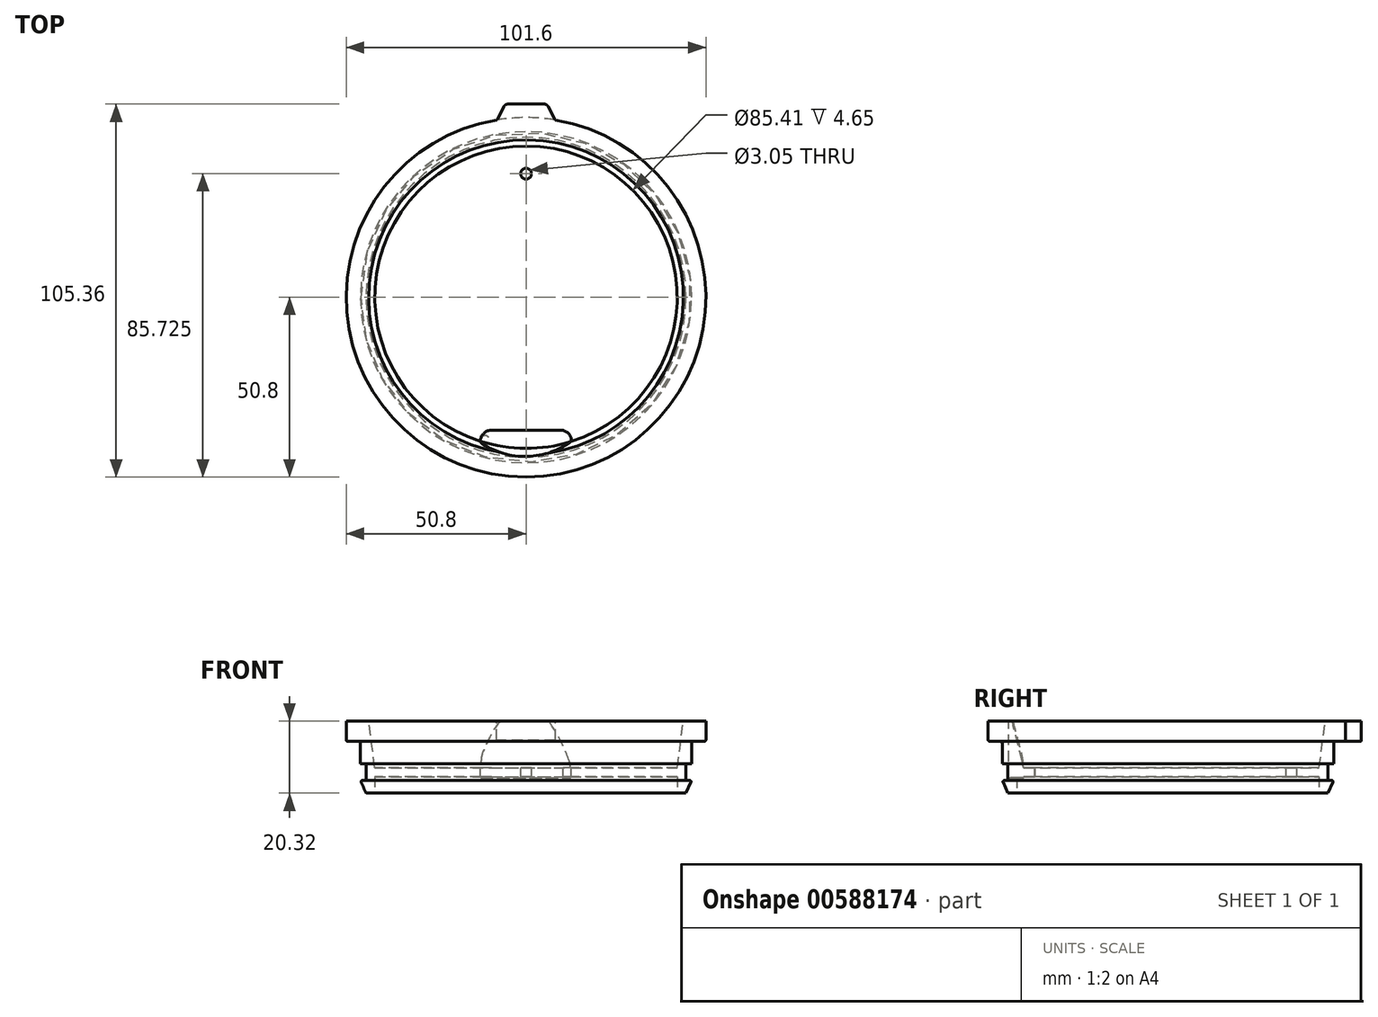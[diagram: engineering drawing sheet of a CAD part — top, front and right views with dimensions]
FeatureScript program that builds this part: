
annotation { "Feature Type Name" : "Feature", "Feature Type Description" : "" }
export const myFeature = defineFeature(function(context is Context, id is Id, definition is map)
    precondition{}
    {
        {
            var Q0;
            Q0=qCreatedBy(makeId("Front.planeOp"),FACE);
            var sketch = newSketch(context, id + "F0", { "sketchPlane" : qUnion([Q0])});
            skLineSegment(sketch, "E0", {"start": v(-44.45, 0) * mm, "end": v(-50.4, 0) * mm});
            skLineSegment(sketch, "E1", {"start": v(-50.8, -0.4) * mm, "end": v(-50.8, -5.24) * mm});
            skLineSegment(sketch, "E2", {"start": v(-50.4, -5.64) * mm, "end": v(-47.56, -5.64) * mm});
            skLineSegment(sketch, "E3", {"start": v(-46.78, -6.43) * mm, "end": v(-46.78, -12) * mm});
            skLineSegment(sketch, "E4", {"start": v(-46.78, -12) * mm, "end": v(-45.19, -12) * mm});
            skLineSegment(sketch, "E5", {"start": v(-45.19, -12) * mm, "end": v(-45.19, -16.76) * mm});
            skLineSegment(sketch, "E6", {"start": v(-45.19, -16.76) * mm, "end": v(-46.3, -16.76) * mm});
            skLineSegment(sketch, "E7", {"start": v(-45.19, -20.32) * mm, "end": v(-42.7, -20.32) * mm});
            skLineSegment(sketch, "E8", {"start": v(0, -20.32) * mm, "end": v(0, 0) * mm});
            skLineSegment(sketch, "E9", {"start": v(-46.58, -17.2) * mm, "end": v(-45.19, -20.32) * mm});
            skPoint(sketch, "E10.visualSharp", {"position": v(-46.78, -16.76) * mm});
            skArc(sketch, "E10.filletArc", {"start": v(-46.3, -16.76) * mm, "mid": v(-46.56, -16.9) * mm, "end": v(-46.58, -17.2) * mm});
            skPoint(sketch, "E11.visualSharp", {"position": v(-46.78, -5.64) * mm});
            skArc(sketch, "E11.filletArc", {"start": v(-46.78, -6.43) * mm, "mid": v(-47, -5.88) * mm, "end": v(-47.56, -5.64) * mm});
            skPoint(sketch, "E12.visualSharp", {"position": v(-50.8, -5.64) * mm});
            skArc(sketch, "E12.filletArc", {"start": v(-50.8, -5.24) * mm, "mid": v(-50.68, -5.53) * mm, "end": v(-50.4, -5.64) * mm});
            skPoint(sketch, "E13.visualSharp", {"position": v(-50.8, 0) * mm});
            skLineSegment(sketch, "E14", {"start": v(-44.45, 0) * mm, "end": v(-42.7, -13.13) * mm});
            skLineSegment(sketch, "E15", {"start": v(-42.7, -13.13) * mm, "end": v(0, -13.13) * mm});
            skLineSegment(sketch, "E16.0", {"start": v(-42.7, -15.67) * mm, "end": v(0, -15.67) * mm});
            skLineSegment(sketch, "E17", {"start": v(-42.7, -15.67) * mm, "end": v(-42.7, -20.32) * mm});
            skLineSegment(sketch, "E18", {"start": v(-50.8, -0.4) * mm, "end": v(-50.8, 0) * mm});
            skLineSegment(sketch, "E19", {"start": v(-50.4, 0) * mm, "end": v(-50.8, 0) * mm});
            skSolve(sketch);
        }
        {
            var Q0;
            Q0 = qSketchRegion(id + "F0", true);
            var Q1;
            Q1=sQuery(id+"F0.wireOp",EDGE,"E8");
            revolve(context, id + "F1", {"entities" : qUnion([Q0]), "axis" : qUnion([Q1]), "revolveType" : RevolveType.FULL});
        }
        {
            var Q0;
            Q0=makeQuery(id+"F1.opRevolve","SWEPT_FACE",FACE,{"disambiguationData":[OSD([sQuery(id+"F0.wireOp",EDGE,"E15")])]});
            cPlane(context, id + "F2", {"entities" : qUnion([Q0]), "cplaneType" : CPlaneType.OFFSET, "offset" : 0 * mm, "oppositeDirection" : true, "width" : 152.4 * mm, "height" : 152.4 * mm});
        }
        {
            var Q0;
            Q0=qCreatedBy(id+"F2.planeOp",FACE);
            var sketch = newSketch(context, id + "F3", { "sketchPlane" : qUnion([Q0])});
            skLineSegment(sketch, "E20", {"start": v(0, 0) * mm, "end": v(0, 34.93) * mm});
            skCircle(sketch, "E21", {"center": v(0, 34.93) * mm, "radius": 1.52 * mm});
            skLineSegment(sketch, "E22", {"start": v(0, 0) * mm, "end": v(0, -42.7) * mm});
            skLineSegment(sketch, "E23.0", {"start": v(-11.11, -37.55) * mm, "end": v(11.11, -37.64) * mm});
            skLineSegment(sketch, "E24", {"start": v(-11.11, -37.55) * mm, "end": v(-11.11, -40.72) * mm, "construction": true});
            skArc(sketch, "E25", {"start": v(-9.72, -37.55) * mm, "mid": v(-11.76, -38.29) * mm, "end": v(-12.86, -40.17) * mm});
            skArc(sketch, "E26.MirrorC", {"start": v(9.02, -37.64) * mm, "mid": v(11.25, -37.94) * mm, "end": v(12.72, -39.66) * mm});
            skPoint(sketch, "E27", {"position": v(-9.73, -43.9) * mm});
            skPoint(sketch, "E28", {"position": v(9.73, -43.9) * mm});
            skPoint(sketch, "E29.start.orphan", {"position": v(9.73, -45.46) * mm});
            skPoint(sketch, "E30.end.orphan", {"position": v(-9.73, -45.46) * mm});
            skArc(sketch, "E31", {"start": v(-12.28, -41.49) * mm, "mid": v(0.02, -44.99) * mm, "end": v(12.22, -41.17) * mm});
            skArc(sketch, "E32.filletArc", {"start": v(-12.86, -40.17) * mm, "mid": v(-12.77, -40.92) * mm, "end": v(-12.28, -41.49) * mm});
            skArc(sketch, "E33.filletArc", {"start": v(12.22, -41.17) * mm, "mid": v(12.73, -40.5) * mm, "end": v(12.72, -39.66) * mm});
            skSolve(sketch);
        }
        {
            var Q0;
            {var subQ0=sQuery(id+"F3.wireOp",EDGE,"E25");Q0=makeQuery(id+"F3.imprint","IMPRINT",FACE,{"disambiguationData":[TD([[makeQuery(id+"F3.imprint","IMPRINT",EDGE,{"derivedFrom":subQ0}),1.0]])]});}
            extrude(context, id + "F4", {"entities" : qUnion([Q0]), "operationType" : NewBodyOperationType.REMOVE, "oppositeDirection" : true, "depth" : 2.8 * mm, "offsetDistance" : 25.4 * mm});
        }
        {
            var Q0;
            Q0 = qSketchRegion(id + "F3", true);
            extrude(context, id + "F5", {"entities" : qUnion([Q0]), "operationType" : NewBodyOperationType.REMOVE, "depth" : 25.4 * mm, "offsetDistance" : 25.4 * mm});
        }
        {
            var Q0;
            Q0=qCreatedBy(id+"F2.planeOp",FACE);
            var sketch = newSketch(context, id + "F6", { "sketchPlane" : qUnion([Q0])});
            skLineSegment(sketch, "E34", {"start": v(0, 34.93) * mm, "end": v(0, 0) * mm, "construction": true});
            skCircle(sketch, "E35", {"center": v(0, 34.93) * mm, "radius": 1.52 * mm});
            skSolve(sketch);
        }
        {
            var Q0;
            Q0 = qSketchRegion(id + "F6", true);
            extrude(context, id + "F7", {"entities" : qUnion([Q0]), "operationType" : NewBodyOperationType.REMOVE, "oppositeDirection" : true, "depth" : 25.4 * mm, "offsetDistance" : 25.4 * mm});
        }
        {
            var Q0;
            Q0=qCreatedBy(makeId("Top.planeOp"),FACE);
            var sketch = newSketch(context, id + "F8", { "sketchPlane" : qUnion([Q0])});
            skLineSegment(sketch, "E36", {"start": v(0, 50.77) * mm, "end": v(0, 54.56) * mm});
            skLineSegment(sketch, "E37", {"start": v(0, 54.56) * mm, "end": v(5.15, 54.56) * mm});
            skLineSegment(sketch, "E38", {"start": v(6.29, 53.87) * mm, "end": v(8.2, 50.1) * mm});
            skLineSegment(sketch, "E39.MirrorCS", {"start": v(0, 54.56) * mm, "end": v(-5.15, 54.56) * mm});
            skLineSegment(sketch, "E40.MirrorCS", {"start": v(-6.29, 53.87) * mm, "end": v(-8.2, 50.1) * mm});
            skArc(sketch, "E41", {"start": v(8.2, 50.1) * mm, "mid": v(0, 50.77) * mm, "end": v(-8.2, 50.1) * mm});
            skLineSegment(sketch, "E42", {"start": v(-8.2, 50.1) * mm, "end": v(-8, 50.48) * mm});
            skLineSegment(sketch, "E43", {"start": v(-8.2, 50.1) * mm, "end": v(-8.63, 50.02) * mm});
            skArc(sketch, "E44", {"start": v(-8.63, 50.02) * mm, "mid": v(-8.26, 50.17) * mm, "end": v(-8, 50.48) * mm});
            skArc(sketch, "E45.MirrorCS", {"start": v(8.63, 50.02) * mm, "mid": v(8.26, 50.17) * mm, "end": v(8, 50.48) * mm});
            skLineSegment(sketch, "E46.MirrorCS", {"start": v(8.2, 50.1) * mm, "end": v(8.63, 50.02) * mm});
            skPoint(sketch, "E47.visualSharp", {"position": v(-5.93, 54.56) * mm});
            skArc(sketch, "E47.filletArc", {"start": v(-5.15, 54.56) * mm, "mid": v(-5.82, 54.38) * mm, "end": v(-6.29, 53.87) * mm});
            skPoint(sketch, "E48.visualSharp", {"position": v(5.93, 54.56) * mm});
            skArc(sketch, "E48.filletArc", {"start": v(6.29, 53.87) * mm, "mid": v(5.82, 54.38) * mm, "end": v(5.15, 54.56) * mm});
            skSolve(sketch);
        }
        {
            var Q0;
            Q0 = qSketchRegion(id + "F8", true);
            extrude(context, id + "F9", {"entities" : qUnion([Q0]), "operationType" : NewBodyOperationType.ADD, "oppositeDirection" : true, "depth" : 5.64 * mm, "offsetDistance" : 25.4 * mm});
        }
    });
